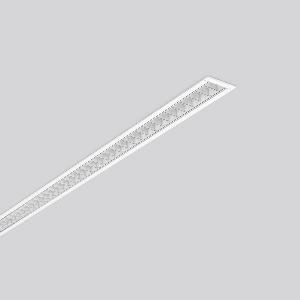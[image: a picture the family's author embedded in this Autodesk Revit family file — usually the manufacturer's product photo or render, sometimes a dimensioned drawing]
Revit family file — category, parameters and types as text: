
# Revit family: less_is_more_27_312179_002_5ece
name_source: partatom
category: Lighting Fixtures
units: mm (PartAtom-declared; Revit-internal decimal feet)

## family parameters
Cut with Voids When Loaded = No
Host = Face
Light Source = No
Part Type = Normal
Room Calculation Point = No
Round Connector Dimension = Use Diameter
Shared = No

## types (1)
- LESS IS MORE 27 (1 x LED Modul 830, 3500 lm, 3000)
    Apparent Load = 43 VA
    CIE Flux Codes = 90 99 100 100 100
    Color Rendering = 80
    Color Temperature = 3000
    Default Elevation = 1800 mm
    Description = Series: LESS IS MORE 27
Recessed ceiling and wall luminaire with slim design. Housing: extruded aluminium profile, powder-coated. End cap aluminium powder-coated. High polish aluminium micro grid. Perfect for office areas (RUG < 19) and environments with computer screens in accordance with EN 12464-1. Suitable for Recessed ceiling mounting, wall (recessed). External driver with connecting cable. 
Colour: traffic white, matt (RAL 9016)
Length: 1514 mm
Width: 38 mm
Height: 2 mm
Cut-out length: 1506 mm
Cut-out width: 30 mm
Recess height: 45-60 mm
Luminaire: recess height: 37 mm
Lamp: LED
Socket: without socket
Colour temperature: 3000K
Colour rendering index (CRI): 82
System power: 43 W
Rated luminous flux: 3500 lm
Luminous efficiency: 81 lm/W
Control gear: Regulated power supply
Protection class: II
Type of protection: IP 20
    Height = 0 mm  [stored 0 ft]
    Lamp = 1 x LED Modul 830
    Lamp Light Flux = 3500 lm
    Lamp count = 1
    Length = 1514 mm
    Lifetime = 50000 h
    Luminous efficacy = 81 lm/W
    Manufacturer = RZB
    ModVariant = No
    Model = 312179.002
    Mounting Place = Ceiling, Wall
    Mounting Type = Recessed
    Number of Poles = 1
    OnlyDefault = Yes
    Power Factor = 1
    Product Name = LESS IS MORE 27
    Product group = Recessed LED linear luminaires
    ProductGroupID = 407
    Protection Class = Protection class II
    Protection Degree = IP 20
    RLX_Detail_Level = 1
    RLX_Emergency_Light_Flux = 0 lm
    RLX_Emergency_Type = 0
    RLX_Emergency_Type_DB = No
    RlxData = <blob elided: 27041 chars, md5=ec0cbcaf>
    Socket = socket
    Standby Power = 0 W
    System Light Flux = 3500 lm
    System Power = 43 W
    Type Comments = Product without accessories
    Type Image = 312177.002.jpg
    URL = http://relux.com
    VarID = ---
    Voltage = 230 V
    Voltage Range = 220-240 V
    Weight = 0.00 kg
    Width = 38 mm

note: [stored X ft] marks values corroborated as IEEE doubles in the binary element streams (Revit-internal decimal feet)

## geometry (parser evidence)
native form markers: Blend x4, Sweep x13
no freeform markers — native parametric forms only
